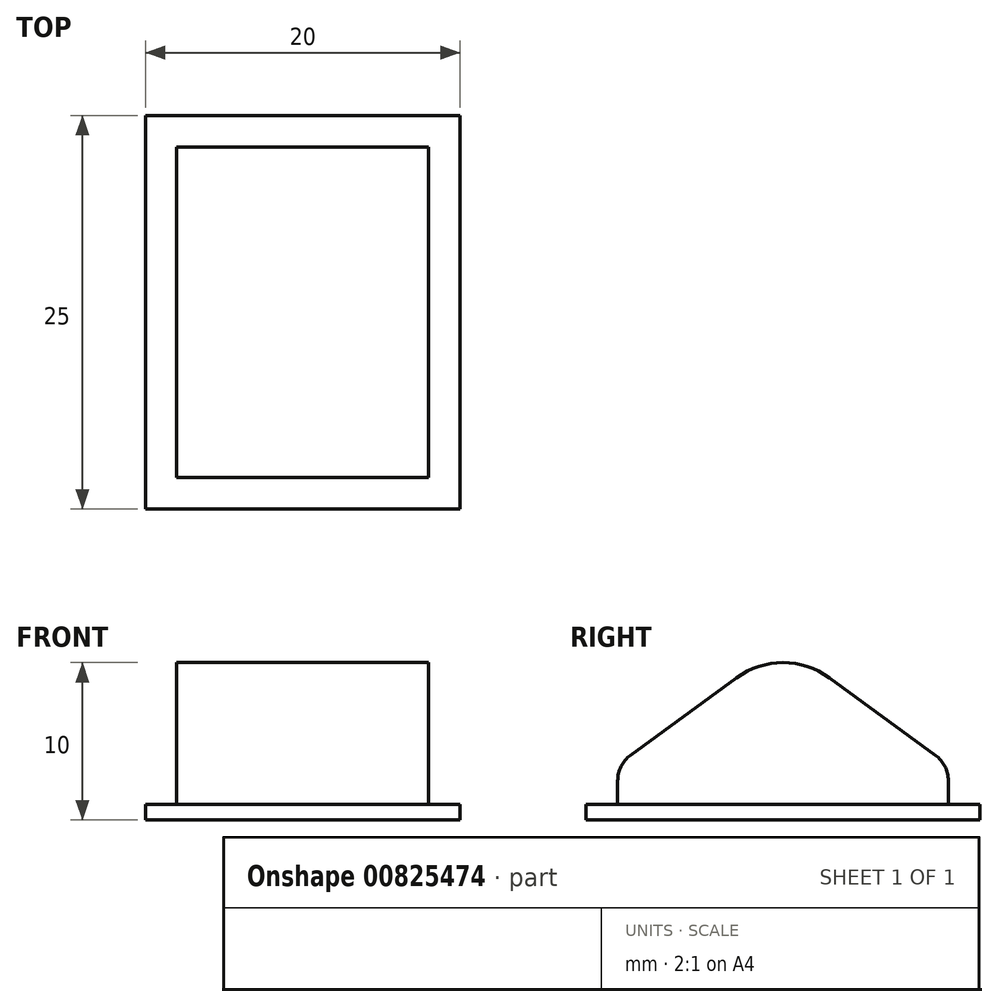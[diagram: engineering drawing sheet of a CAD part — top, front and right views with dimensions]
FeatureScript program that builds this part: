
annotation { "Feature Type Name" : "Feature", "Feature Type Description" : "" }
export const myFeature = defineFeature(function(context is Context, id is Id, definition is map)
    precondition{}
    {
        {
            var Q0;
            Q0=qCreatedBy(makeId("Top.planeOp"),FACE);
            var sketch = newSketch(context, id + "F0", { "sketchPlane" : qUnion([Q0])});
            skLineSegment(sketch, "E0.bottom", {"start": v(10, -12.5) * mm, "end": v(-10, -12.5) * mm});
            skLineSegment(sketch, "E0.top", {"start": v(10, 12.5) * mm, "end": v(-10, 12.5) * mm});
            skLineSegment(sketch, "E0.left", {"start": v(10, -12.5) * mm, "end": v(10, 12.5) * mm});
            skLineSegment(sketch, "E0.right", {"start": v(-10, -12.5) * mm, "end": v(-10, 12.5) * mm});
            skPoint(sketch, "E0.middle", {"position": v(0, 0) * mm});
            skSolve(sketch);
        }
        {
            var Q0;
            Q0=makeQuery(id+"F0.imprint","IMPRINT",FACE,{"disambiguationData":[TD([[makeQuery(id+"F0.imprint","IMPRINT",EDGE,{"derivedFrom":sQuery(id+"F0.wireOp",EDGE,"E0.bottom")}),-1.0]])]});
            extrude(context, id + "F1", {"entities" : qUnion([Q0]), "depth" : 1 * mm, "offsetDistance" : 25 * mm});
        }
        {
            var Q0;
            Q0=qCreatedBy(makeId("Right.planeOp"),FACE);
            var sketch = newSketch(context, id + "F2", { "sketchPlane" : qUnion([Q0])});
            skArc(sketch, "E1", {"start": v(2.95, 9.04) * mm, "mid": v(0, 10) * mm, "end": v(-2.95, 9.04) * mm});
            skArc(sketch, "E2", {"start": v(-9.68, 4.11) * mm, "mid": v(-10.28, 3.4) * mm, "end": v(-10.5, 2.5) * mm});
            skArc(sketch, "E3", {"start": v(10.5, 2.5) * mm, "mid": v(10.28, 3.4) * mm, "end": v(9.68, 4.11) * mm});
            skLineSegment(sketch, "E4", {"start": v(-9.68, 4.11) * mm, "end": v(-2.95, 9.04) * mm});
            skLineSegment(sketch, "E5", {"start": v(2.95, 9.04) * mm, "end": v(9.68, 4.11) * mm});
            skLineSegment(sketch, "E6", {"start": v(10.5, 2.5) * mm, "end": v(10.5, 1) * mm});
            skLineSegment(sketch, "E7", {"start": v(-10.5, 2.5) * mm, "end": v(-10.5, 1) * mm});
            skLineSegment(sketch, "E8", {"start": v(10.5, 1) * mm, "end": v(-10.5, 1) * mm});
            skSolve(sketch);
        }
        {
            var Q0;
            Q0=makeQuery(id+"F2.imprint","IMPRINT",FACE,{"disambiguationData":[TD([[makeQuery(id+"F2.imprint","IMPRINT",EDGE,{"derivedFrom":sQuery(id+"F2.wireOp",EDGE,"E1")}),1.0]])]});
            extrude(context, id + "F3", {"entities" : qUnion([Q0]), "operationType" : NewBodyOperationType.ADD, "endBound" : BoundingType.SYMMETRIC, "depth" : 16 * mm, "offsetDistance" : 25 * mm});
        }
    });
